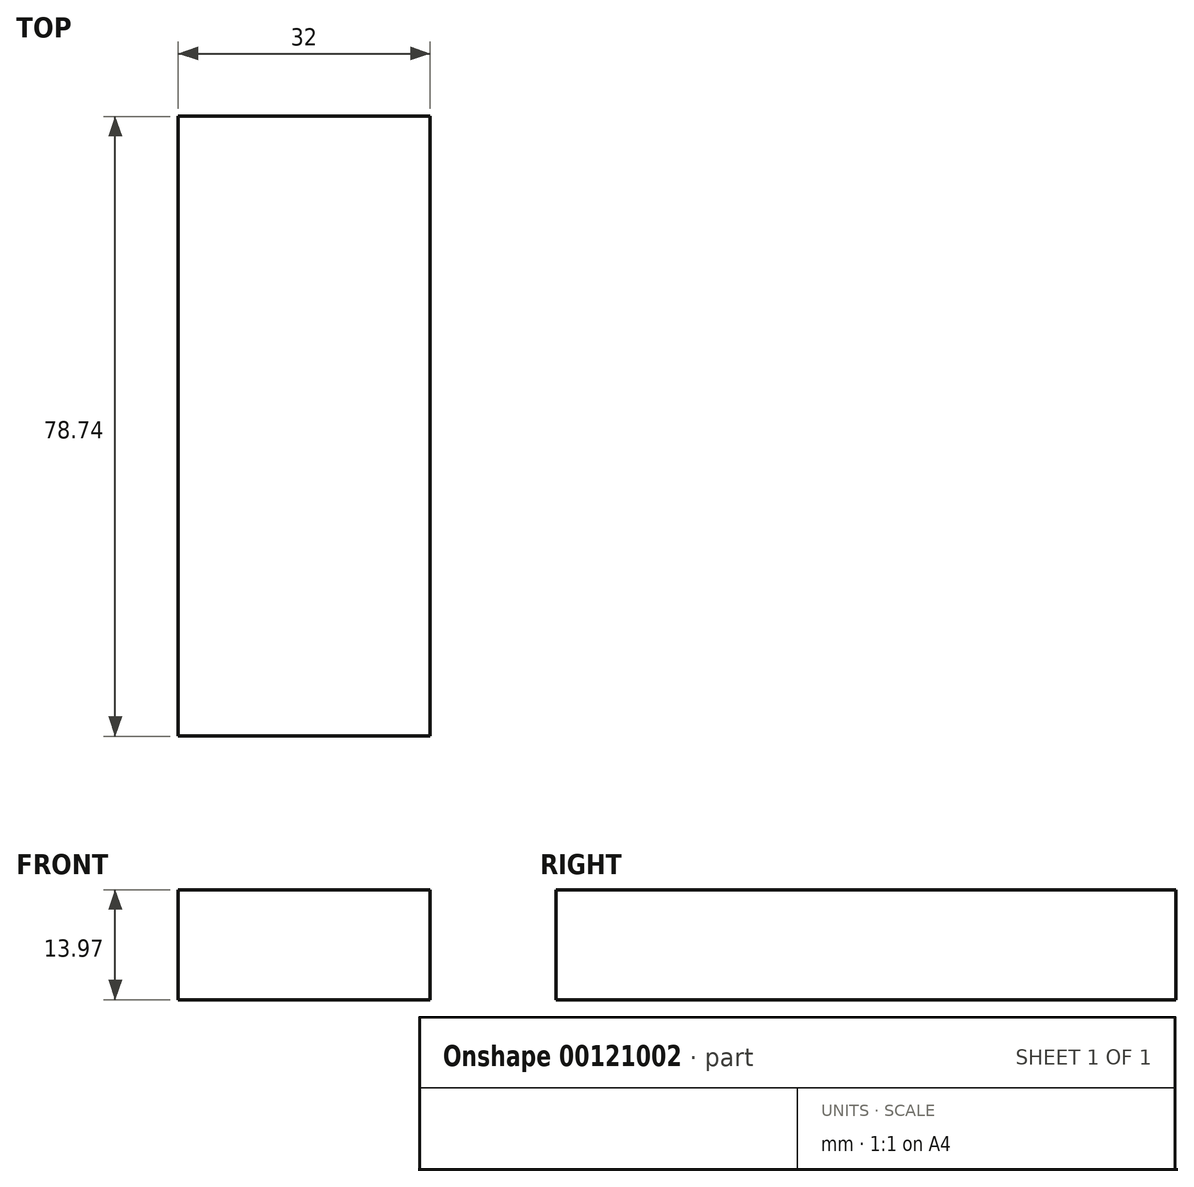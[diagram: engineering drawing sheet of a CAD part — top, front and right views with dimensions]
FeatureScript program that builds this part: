
annotation { "Feature Type Name" : "Feature", "Feature Type Description" : "" }
export const myFeature = defineFeature(function(context is Context, id is Id, definition is map)
    precondition{}
    {
        {
            var Q0;
            Q0=qCreatedBy(makeId("Top.planeOp"),FACE);
            var sketch = newSketch(context, id + "F0", { "sketchPlane" : qUnion([Q0])});
            skLineSegment(sketch, "E0.bottom", {"start": v(-13.16, -24.24) * mm, "end": v(18.84, -24.24) * mm});
            skLineSegment(sketch, "E0.top", {"start": v(-13.16, 54.5) * mm, "end": v(18.84, 54.5) * mm});
            skLineSegment(sketch, "E0.left", {"start": v(-13.16, -24.24) * mm, "end": v(-13.16, 54.5) * mm});
            skLineSegment(sketch, "E0.right", {"start": v(18.84, -24.24) * mm, "end": v(18.84, 54.5) * mm});
            skSolve(sketch);
        }
        {
            var Q0;
            Q0=qSketchRegion(id+"F0",true);
            extrude(context, id + "F1", {"entities" : qUnion([Q0]), "depth" : 13.97 * mm});
        }
    });
